AUTODESK INVENTOR PART (.ipt)
format: ipt  version: 2021 (Build 250183000, 183)  size: 134,656 bytes
history: native  units: mm
features: other x13, extrude x1, sketch x1, reference x1
ambient origin geometry x8: Origin, YZ Plane, XZ Plane, XY Plane, X Axis, Y Axis, Z Axis, Center Point
bodies: Body1 (feature_tree)
feature tree (16):
  other  "Bryła1"
  other  "Płaszczyzna konstrukcyjna1"
  other  "LUW1"
  extrude  "Wyciągnięcie proste1"  Depth=15.0mm
  sketch  "Szkic1"
  reference  "Odniesienie1"
  other  "LUW1: Płaszczyzna YZ"
  other  "LUW1: Płaszczyzna XZ"
  other  "LUW1: Płaszczyzna XY"
  other  "LUW1: Oś X"
  other  "LUW1: Oś Y"
  other  "LUW1: Oś Z"
  other  "LUW1: Punkt środkowy"
  parser-record x1  (decoder bookkeeping rows leaked as tree rows — omitted from the tree; the rows remain in map.json)
  other  "zespolokno.iam"
  other  "alu:1"
note: 1 file-system path scrubbed to <path> (originals preserved in map.json)
